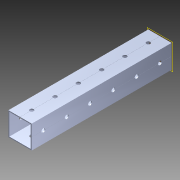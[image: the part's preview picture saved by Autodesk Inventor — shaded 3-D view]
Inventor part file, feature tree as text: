
AUTODESK INVENTOR PART (.ipt)
format: ipt  version: 2014 (Build 180170000, 170)  size: 1,147,392 bytes
history: native  units: in
note: dims shown in document units (in); Inventor stores cm internally (conversion verified against a paired STEP export)
features: pattern_circular x1, other x1, plane x1, extrude x1, imported_body x1, sketch x1
ambient origin geometry x8: Origin, YZ Plane, XZ Plane, XY Plane, X Axis, Y Axis, Z Axis, Center Point
bodies: Body1 (feature_tree)
feature tree (6):
  pattern_circular  "CirPattern2"
  other  "217-3426-STEP1"
  plane  "Work Plane1"
  extrude  "Extrusion1"  Depth=3937.0079in TaperAngle=0.0deg
  imported_body  "Base1"
  sketch  "Sketch1"  dims[d0=-6.0in d1=3937.0079in d2=0.0in]
